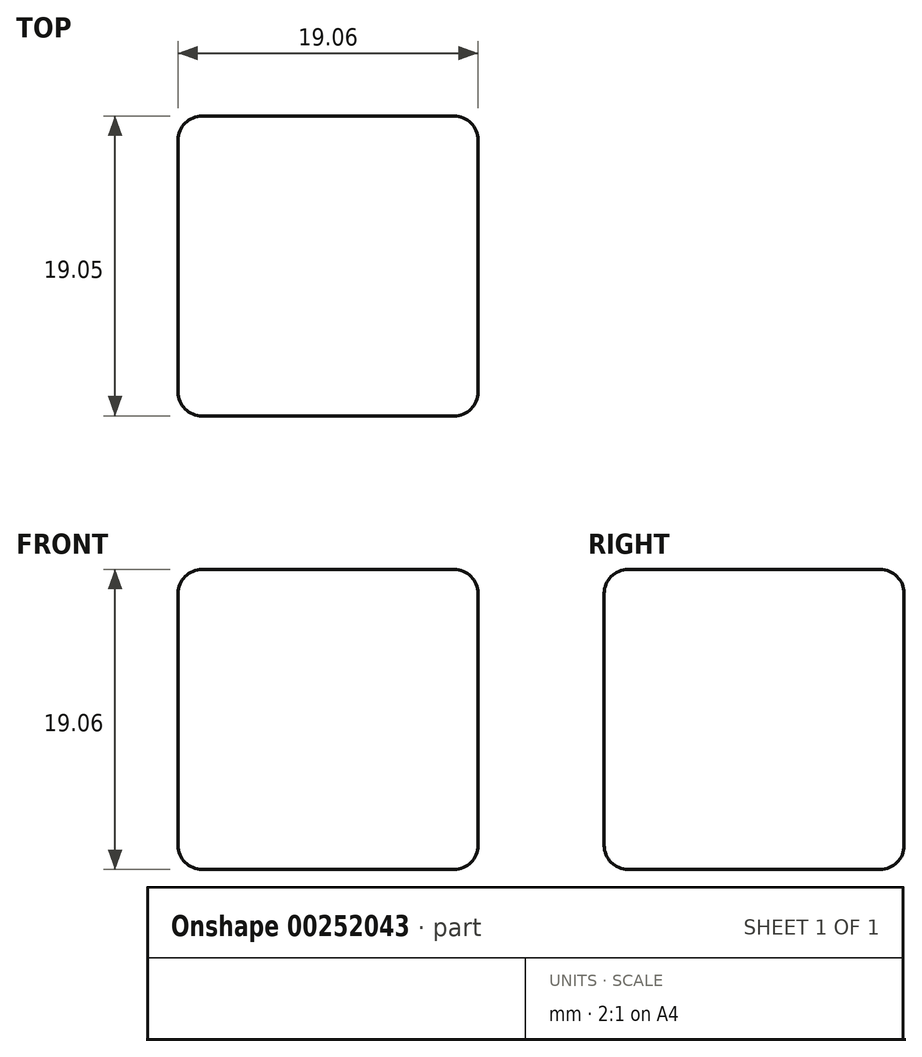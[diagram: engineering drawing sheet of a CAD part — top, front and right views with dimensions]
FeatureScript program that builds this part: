
annotation { "Feature Type Name" : "Feature", "Feature Type Description" : "" }
export const myFeature = defineFeature(function(context is Context, id is Id, definition is map)
    precondition{}
    {
        {
            var Q0;
            Q0=qCreatedBy(makeId("Front.planeOp"),FACE);
            var sketch = newSketch(context, id + "F0", { "sketchPlane" : qUnion([Q0])});
            skLineSegment(sketch, "E0.bottom", {"start": v(-9.53, -9.52) * mm, "end": v(9.53, -9.52) * mm});
            skLineSegment(sketch, "E0.top", {"start": v(-9.53, 9.52) * mm, "end": v(9.52, 9.52) * mm});
            skLineSegment(sketch, "E0.left", {"start": v(-9.52, -9.52) * mm, "end": v(-9.53, 9.52) * mm});
            skLineSegment(sketch, "E0.right", {"start": v(9.53, -9.52) * mm, "end": v(9.52, 9.52) * mm});
            skPoint(sketch, "E0.middle", {"position": v(0, 0) * mm});
            skSolve(sketch);
        }
        {
            var Q0;
            Q0=makeQuery(id+"F0.imprint","IMPRINT",FACE,{"disambiguationData":[TD([[makeQuery(id+"F0.imprint","IMPRINT",EDGE,{"derivedFrom":sQuery(id+"F0.wireOp",EDGE,"E0.bottom")}),1.0]])]});
            extrude(context, id + "F1", {"entities" : qUnion([Q0]), "depth" : 19.05 * mm});
        }
        {
            var Q0;
            Q0=makeQuery(id+"F1.opExtrude","CAP_EDGE",EDGE,{"disambiguationData":[OSD([sQuery(id+"F0.wireOp",EDGE,"E0.top")])],"isStart":true});
            var Q1;
            Q1=makeQuery(id+"F1.opExtrude","CAP_EDGE",EDGE,{"disambiguationData":[OSD([sQuery(id+"F0.wireOp",EDGE,"E0.top")])],"isStart":false});
            var Q2;
            Q2=makeQuery(id+"F1.opExtrude","SWEPT_EDGE",EDGE,{"disambiguationData":[OSD([sQuery(id+"F0.wireOp",EDGE,"E0.top"),sQuery(id+"F0.wireOp",EDGE,"E0.left")])]});
            var Q3;
            Q3=makeQuery(id+"F1.opExtrude","SWEPT_EDGE",EDGE,{"disambiguationData":[OSD([sQuery(id+"F0.wireOp",EDGE,"E0.top"),sQuery(id+"F0.wireOp",EDGE,"E0.right")])]});
            var Q4;
            Q4=makeQuery(id+"F1.opExtrude","CAP_EDGE",EDGE,{"disambiguationData":[OSD([sQuery(id+"F0.wireOp",EDGE,"E0.bottom")])],"isStart":true});
            var Q5;
            Q5=makeQuery(id+"F1.opExtrude","CAP_EDGE",EDGE,{"disambiguationData":[OSD([sQuery(id+"F0.wireOp",EDGE,"E0.right")])],"isStart":true});
            var Q6;
            Q6=makeQuery(id+"F1.opExtrude","CAP_EDGE",EDGE,{"disambiguationData":[OSD([sQuery(id+"F0.wireOp",EDGE,"E0.right")])],"isStart":false});
            var Q7;
            Q7=makeQuery(id+"F1.opExtrude","SWEPT_EDGE",EDGE,{"disambiguationData":[OSD([sQuery(id+"F0.wireOp",EDGE,"E0.bottom"),sQuery(id+"F0.wireOp",EDGE,"E0.right")])]});
            var Q8;
            Q8=makeQuery(id+"F1.opExtrude","CAP_EDGE",EDGE,{"disambiguationData":[OSD([sQuery(id+"F0.wireOp",EDGE,"E0.bottom")])],"isStart":false});
            var Q9;
            Q9=makeQuery(id+"F1.opExtrude","CAP_EDGE",EDGE,{"disambiguationData":[OSD([sQuery(id+"F0.wireOp",EDGE,"E0.left")])],"isStart":false});
            var Q10;
            Q10=makeQuery(id+"F1.opExtrude","SWEPT_EDGE",EDGE,{"disambiguationData":[OSD([sQuery(id+"F0.wireOp",EDGE,"E0.bottom"),sQuery(id+"F0.wireOp",EDGE,"E0.left")])]});
            var Q11;
            Q11=makeQuery(id+"F1.opExtrude","CAP_EDGE",EDGE,{"disambiguationData":[OSD([sQuery(id+"F0.wireOp",EDGE,"E0.left")])],"isStart":true});
            fillet(context, id + "F2", {"entities" : qUnion([Q0, Q1, Q2, Q3, Q4, Q5, Q6, Q7, Q8, Q9, Q10, Q11]), "radius" : 1.52 * mm, "tangentPropagation" : true, "allowEdgeOverflow" : false});
        }
    });
